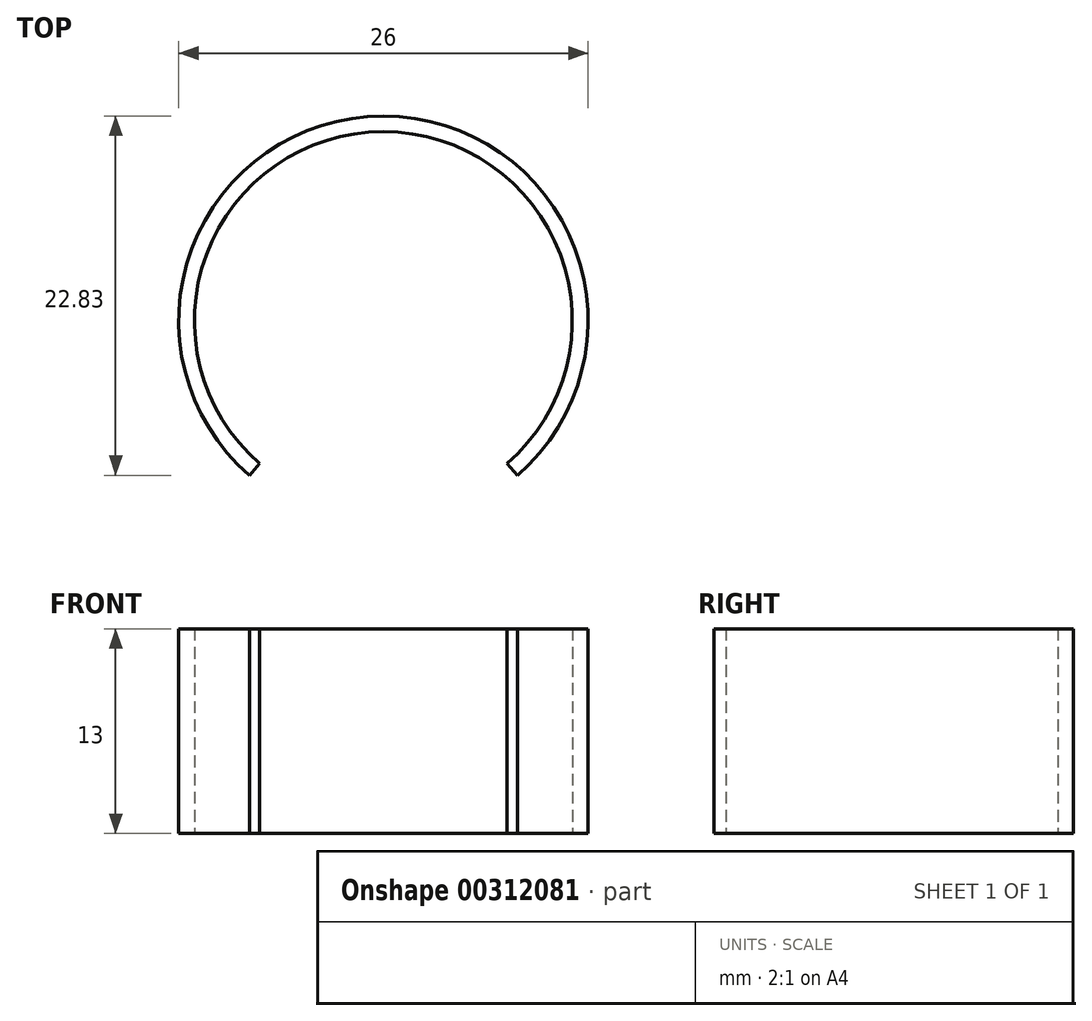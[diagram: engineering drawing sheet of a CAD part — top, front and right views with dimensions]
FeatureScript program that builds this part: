
annotation { "Feature Type Name" : "Feature", "Feature Type Description" : "" }
export const myFeature = defineFeature(function(context is Context, id is Id, definition is map)
    precondition{}
    {
        {
            var Q0;
            Q0=qCreatedBy(makeId("Top.planeOp"),FACE);
            var sketch = newSketch(context, id + "F0", { "sketchPlane" : qUnion([Q0])});
            skArc(sketch, "E0", {"start": v(15.72, 0) * mm, "mid": v(7.86, 21.07) * mm, "end": v(0, 0) * mm});
            skArc(sketch, "E1.0", {"start": v(16.37, -0.76) * mm, "mid": v(7.86, 22.07) * mm, "end": v(-0.65, -0.76) * mm});
            skLineSegment(sketch, "E2", {"start": v(-0.65, -0.76) * mm, "end": v(0, 0) * mm});
            skLineSegment(sketch, "E3", {"start": v(16.37, -0.76) * mm, "end": v(15.72, 0) * mm});
            skSolve(sketch);
        }
        {
            var Q0;
            Q0=makeQuery(id+"F0.imprint","IMPRINT",FACE,{"disambiguationData":[TD([[makeQuery(id+"F0.imprint","IMPRINT",EDGE,{"derivedFrom":sQuery(id+"F0.wireOp",EDGE,"E0")}),-1.0]])]});
            extrude(context, id + "F1", {"entities" : qUnion([Q0]), "depth" : 13 * mm});
        }
    });
